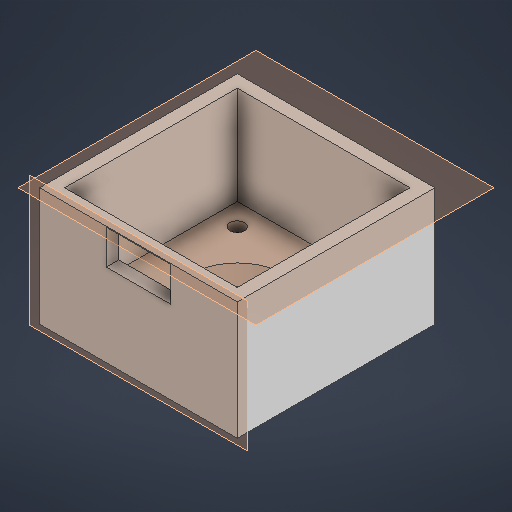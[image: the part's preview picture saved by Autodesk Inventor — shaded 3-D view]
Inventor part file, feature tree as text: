
AUTODESK INVENTOR PART (.ipt)
format: ipt  version: 2025.2 (Build 292293000, 293)  size: 230,912 bytes
history: native  units: mm
features: sketch x5, other x4, extrude x3, hole x2
ambient origin geometry x8: Origin, YZ Plane, XZ Plane, XY Plane, X Axis, Y Axis, Z Axis, Center Point
bodies: Body1 (feature_tree)
feature tree (14):
  other  "ソリッド1"
  extrude  "押し出し1"  Depth=47.5mm
  other  "作業平面1"
  extrude  "押し出し3"  Depth=47.5mm
  other  "作業平面2"
  hole  "穴1"  [1 undecoded]
  hole  "穴2"  [1 undecoded]
  other  "作業平面3"
  extrude  "押し出し4"  Depth=41.5mm
  sketch  "スケッチ1"
  sketch  "スケッチ3"
  sketch  "スケッチ4"
  sketch  "スケッチ5"
  sketch  "スケッチ6"
note: 2 required parameter values undecoded (feature->parameter linkage not recoverable at this tier; creation-order binding heuristic only, values carry confidence <= 0.55)
